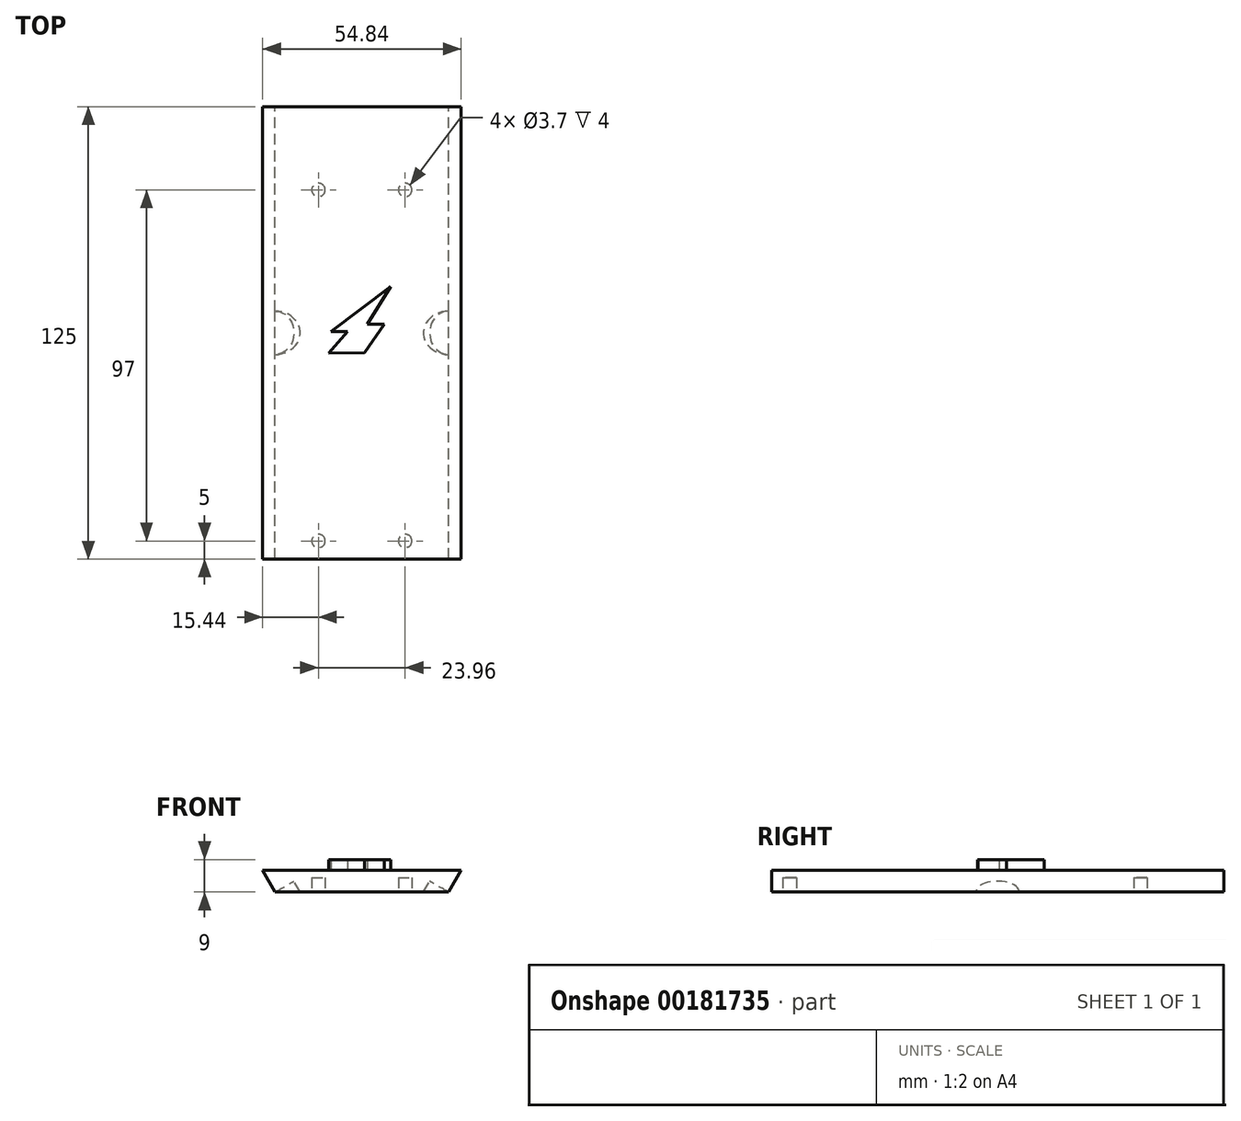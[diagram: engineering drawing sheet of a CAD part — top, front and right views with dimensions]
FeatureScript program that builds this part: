
annotation { "Feature Type Name" : "Feature", "Feature Type Description" : "" }
export const myFeature = defineFeature(function(context is Context, id is Id, definition is map)
    precondition{}
    {
        {
            var Q0;
            Q0=qCreatedBy(makeId("Front.planeOp"),FACE);
            var sketch = newSketch(context, id + "F0", { "sketchPlane" : qUnion([Q0])});
            skCircle(sketch, "E0.cCircle", {"center": v(0, 0) * mm, "radius": 47.5 * mm, "construction": true});
            skLineSegment(sketch, "E0.0", {"start": v(-27.42, -47.5) * mm, "end": v(-54.85, 0) * mm});
            skLineSegment(sketch, "E0.1", {"start": v(-54.85, 0) * mm, "end": v(-27.42, 47.5) * mm});
            skLineSegment(sketch, "E0.2", {"start": v(-27.42, 47.5) * mm, "end": v(27.42, 47.5) * mm});
            skLineSegment(sketch, "E0.3", {"start": v(27.42, 47.5) * mm, "end": v(54.85, 0) * mm});
            skLineSegment(sketch, "E0.4", {"start": v(54.85, 0) * mm, "end": v(27.42, -47.5) * mm});
            skLineSegment(sketch, "E0.5", {"start": v(27.42, -47.5) * mm, "end": v(-27.42, -47.5) * mm});
            skPoint(sketch, "E0.0.midPoint", {"position": v(-41.14, -23.75) * mm});
            skCircle(sketch, "E1.cCircle", {"center": v(0, 0) * mm, "radius": 41.5 * mm, "construction": true});
            skLineSegment(sketch, "E1.0", {"start": v(-23.96, -41.5) * mm, "end": v(-47.92, 0) * mm});
            skLineSegment(sketch, "E1.1", {"start": v(-47.92, 0) * mm, "end": v(-23.96, 41.5) * mm});
            skLineSegment(sketch, "E1.2", {"start": v(-23.96, 41.5) * mm, "end": v(23.96, 41.5) * mm});
            skLineSegment(sketch, "E1.3", {"start": v(23.96, 41.5) * mm, "end": v(47.92, 0) * mm});
            skLineSegment(sketch, "E1.4", {"start": v(47.92, 0) * mm, "end": v(23.96, -41.5) * mm});
            skLineSegment(sketch, "E1.5", {"start": v(23.96, -41.5) * mm, "end": v(-23.96, -41.5) * mm});
            skPoint(sketch, "E1.0.midPoint", {"position": v(-35.94, -20.75) * mm});
            skLineSegment(sketch, "E2", {"start": v(27.42, 47.5) * mm, "end": v(23.96, 41.5) * mm});
            skLineSegment(sketch, "E3", {"start": v(-27.42, 47.5) * mm, "end": v(-23.96, 41.5) * mm});
            skSolve(sketch);
        }
        {
            var Q0;
            Q0=makeQuery(id+"F0.imprint","IMPRINT",FACE,{"disambiguationData":[TD([[makeQuery(id+"F0.imprint","IMPRINT",EDGE,{"derivedFrom":sQuery(id+"F0.wireOp",EDGE,"E0.2")}),-1.0]])]});
            extrude(context, id + "F1", {"entities" : qUnion([Q0]), "depth" : 125 * mm});
        }
        {
            var Q0;
            Q0=makeQuery(id+"F1.opExtrude","SWEPT_FACE",FACE,{"disambiguationData":[OSD([sQuery(id+"F0.wireOp",EDGE,"E1.2")])]});
            var sketch = newSketch(context, id + "F2", { "sketchPlane" : qUnion([Q0])});
            skPoint(sketch, "E4", {"position": v(0, 125) * mm});
            skPoint(sketch, "E5", {"position": v(0, 120) * mm});
            skLineSegment(sketch, "E6", {"start": v(0, 120) * mm, "end": v(-23.96, 120) * mm});
            skPoint(sketch, "E7", {"position": v(-11.98, 120) * mm});
            skCircle(sketch, "E8", {"center": v(-11.98, 120) * mm, "radius": 1.85 * mm});
            skCircle(sketch, "E9.MirrorC", {"center": v(11.98, 120) * mm, "radius": 1.85 * mm});
            skPoint(sketch, "E10", {"position": v(0, 23) * mm});
            skLineSegment(sketch, "E11", {"start": v(0, 23) * mm, "end": v(-23.96, 23) * mm});
            skPoint(sketch, "E12", {"position": v(-11.98, 23) * mm});
            skCircle(sketch, "E13", {"center": v(-11.98, 23) * mm, "radius": 1.85 * mm});
            skCircle(sketch, "E14.MirrorC", {"center": v(11.98, 23) * mm, "radius": 1.85 * mm});
            skSolve(sketch);
        }
        {
            var Q0;
            Q0=qSketchRegion(id+"F2",true);
            extrude(context, id + "F3", {"entities" : qUnion([Q0]), "operationType" : NewBodyOperationType.REMOVE, "oppositeDirection" : true, "depth" : 4 * mm});
        }
        {
            var Q0;
            Q0=makeQuery(id+"F1.opExtrude","SWEPT_FACE",FACE,{"disambiguationData":[OSD([sQuery(id+"F0.wireOp",EDGE,"E0.2")])]});
            var sketch = newSketch(context, id + "F4", { "sketchPlane" : qUnion([Q0])});
            skPoint(sketch, "E15", {"position": v(-23.96, -62.5) * mm});
            skPoint(sketch, "E16", {"position": v(0, -90) * mm});
            skPoint(sketch, "E17", {"position": v(0, -62.5) * mm});
            skLineSegment(sketch, "E18.bottom", {"start": v(-11, -49.59) * mm, "end": v(9, -49.59) * mm});
            skLineSegment(sketch, "E18.top", {"start": v(-11, -69.59) * mm, "end": v(9, -69.59) * mm});
            skLineSegment(sketch, "E18.left", {"start": v(-11, -49.59) * mm, "end": v(-11, -69.59) * mm});
            skLineSegment(sketch, "E18.right", {"start": v(9, -49.59) * mm, "end": v(9, -69.59) * mm});
            skPoint(sketch, "E19", {"position": v(-1, -49.59) * mm});
            skPoint(sketch, "E20", {"position": v(9, -59.59) * mm});
            skLineSegment(sketch, "E21", {"start": v(-9.2, -68.07) * mm, "end": v(-3.97, -62.14) * mm});
            skLineSegment(sketch, "E22", {"start": v(-3.97, -62.14) * mm, "end": v(-8.47, -62.14) * mm});
            skLineSegment(sketch, "E23", {"start": v(-8.47, -62.14) * mm, "end": v(7.94, -49.65) * mm});
            skLineSegment(sketch, "E24", {"start": v(7.94, -49.65) * mm, "end": v(1.48, -60.1) * mm});
            skLineSegment(sketch, "E25", {"start": v(1.48, -60.1) * mm, "end": v(6.25, -60.1) * mm});
            skLineSegment(sketch, "E26", {"start": v(6.25, -60.1) * mm, "end": v(0.69, -67.93) * mm});
            skLineSegment(sketch, "E27", {"start": v(0.69, -67.93) * mm, "end": v(-9.2, -68.07) * mm});
            skSolve(sketch);
        }
        {
            var Q0;
            Q0=makeQuery(id+"F4.imprint","IMPRINT",FACE,{"disambiguationData":[TD([[makeQuery(id+"F4.imprint","IMPRINT",EDGE,{"derivedFrom":sQuery(id+"F4.wireOp",EDGE,"E21")}),-1.0]])]});
            extrude(context, id + "F5", {"entities" : qUnion([Q0]), "operationType" : NewBodyOperationType.ADD, "depth" : 3 * mm});
        }
        {
            var Q0;
            Q0=makeQuery(id+"F1.opExtrude","SWEPT_EDGE",EDGE,{"disambiguationData":[OSD([sQuery(id+"F0.wireOp",EDGE,"E1.1"),sQuery(id+"F0.wireOp",EDGE,"E1.2"),sQuery(id+"F0.wireOp",EDGE,"E3")])]});
            cPlane(context, id + "F6", {"entities" : qUnion([Q0]), "cplaneType" : CPlaneType.LINE_ANGLE, "offset" : 25 * mm, "angle" : 150 * degree, "width" : 150 * mm, "height" : 150 * mm});
        }
        {
            var Q0;
            Q0=qCreatedBy(id+"F6.planeOp",FACE);
            var sketch = newSketch(context, id + "F7", { "sketchPlane" : qUnion([Q0])});
            skCircle(sketch, "E28", {"center": v(0, 62.5) * mm, "radius": 6 * mm});
            skSolve(sketch);
        }
        {
            var Q0;
            Q0=qSketchRegion(id+"F7",true);
            extrude(context, id + "F8", {"entities" : qUnion([Q0]), "operationType" : NewBodyOperationType.REMOVE, "depth" : 25 * mm});
        }
        {
            var Q0;
            Q0=makeQuery(id+"F1.opExtrude","SWEPT_EDGE",EDGE,{"disambiguationData":[OSD([sQuery(id+"F0.wireOp",EDGE,"E1.2"),sQuery(id+"F0.wireOp",EDGE,"E1.3"),sQuery(id+"F0.wireOp",EDGE,"E2")])]});
            cPlane(context, id + "F9", {"entities" : qUnion([Q0]), "cplaneType" : CPlaneType.LINE_ANGLE, "offset" : 25 * mm, "angle" : 30 * degree, "width" : 150 * mm, "height" : 150 * mm});
        }
        {
            var Q0;
            Q0=qCreatedBy(id+"F9.planeOp",FACE);
            var sketch = newSketch(context, id + "F10", { "sketchPlane" : qUnion([Q0])});
            skCircle(sketch, "E29", {"center": v(0, -62.5) * mm, "radius": 6 * mm});
            skSolve(sketch);
        }
        {
            var Q0;
            Q0=qSketchRegion(id+"F10",true);
            extrude(context, id + "F11", {"entities" : qUnion([Q0]), "operationType" : NewBodyOperationType.REMOVE, "oppositeDirection" : true, "depth" : 25 * mm});
        }
    });
